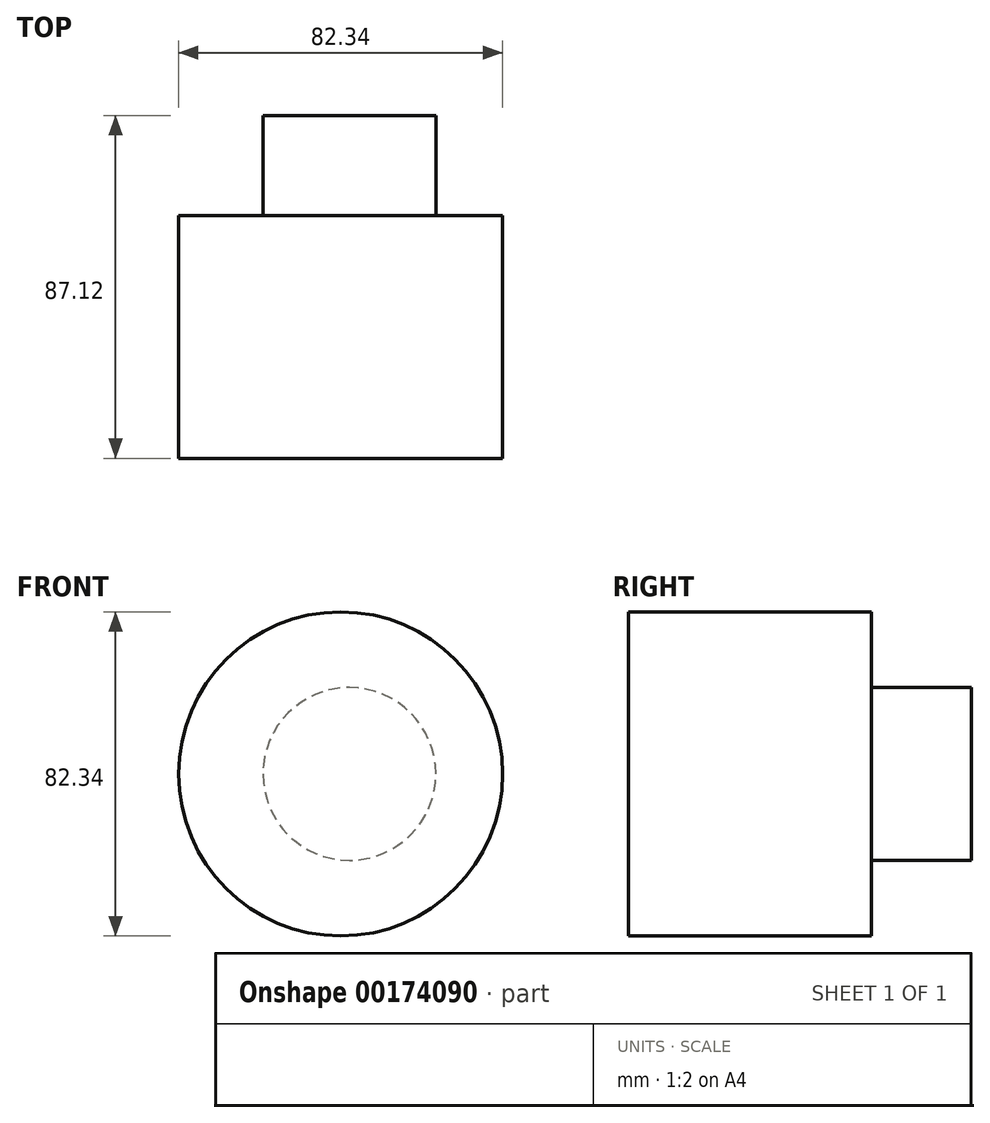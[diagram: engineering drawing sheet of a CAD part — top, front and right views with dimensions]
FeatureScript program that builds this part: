
annotation { "Feature Type Name" : "Feature", "Feature Type Description" : "" }
export const myFeature = defineFeature(function(context is Context, id is Id, definition is map)
    precondition{}
    {
        {
            var Q0;
            Q0=qCreatedBy(makeId("Front.planeOp"),FACE);
            var sketch = newSketch(context, id + "F0", { "sketchPlane" : qUnion([Q0])});
            skCircle(sketch, "E0", {"center": v(0, 0) * mm, "radius": 41.17 * mm});
            skSolve(sketch);
        }
        {
            var Q0;
            Q0=makeQuery(id+"F0.imprint","IMPRINT",FACE,{"disambiguationData":[TD([[makeQuery(id+"F0.imprint","IMPRINT",EDGE,{"derivedFrom":sQuery(id+"F0.wireOp",EDGE,"E0")}),1.0]])]});
            extrude(context, id + "F1", {"entities" : qUnion([Q0]), "depth" : 61.72 * mm});
        }
        {
            var Q0;
            Q0=qCreatedBy(makeId("Front.planeOp"),FACE);
            var sketch = newSketch(context, id + "F2", { "sketchPlane" : qUnion([Q0])});
            skCircle(sketch, "E1", {"center": v(2.2, 0) * mm, "radius": 21.96 * mm});
            skSolve(sketch);
        }
        {
            var Q0;
            Q0 = qSketchRegion(id + "F2", true);
            var Q1;
            Q1=makeQuery(id+"F1.opExtrude","CAP_FACE",FACE,{"disambiguationData":[OSD([sQuery(id+"F0.wireOp",EDGE,"E0")])],"isStart":false});
            extrude(context, id + "F3", {"entities" : qUnion([Q0, Q1]), "operationType" : NewBodyOperationType.ADD, "oppositeDirection" : true, "depth" : 25.4 * mm});
        }
    });
